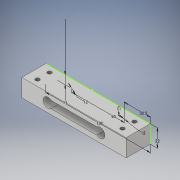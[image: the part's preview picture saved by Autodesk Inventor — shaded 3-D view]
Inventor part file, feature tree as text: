
AUTODESK INVENTOR PART (.ipt)
format: ipt  version: 2019 (Build 230136000, 136)  size: 134,656 bytes
history: native  units: mm
features: sketch x2, extrude x2, other x1, hole x1
ambient origin geometry x8: Origin, YZ Plane, XZ Plane, XY Plane, X Axis, Y Axis, Z Axis, Center Point
bodies: Body1 (feature_tree)
feature tree (6):
  other  "ソリッド1"
  sketch  "スケッチ1"
  extrude  "押し出し1"  Depth=130.0mm
  extrude  "押し出し2"  Depth=22.0mm
  hole  "穴1"  [1 undecoded]
  sketch  "スケッチ2"
note: 1 required parameter value undecoded (feature->parameter linkage not recoverable at this tier; creation-order binding heuristic only, values carry confidence <= 0.55)
